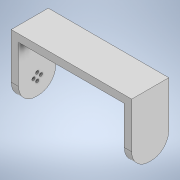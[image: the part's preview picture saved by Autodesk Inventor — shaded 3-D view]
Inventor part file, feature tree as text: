
AUTODESK INVENTOR PART (.ipt)
format: ipt  version: 2022 (Build 260153000, 153)  size: 152,064 bytes
history: native  units: mm
features: extrude x5, sketch x5, fillet x1
ambient origin geometry x8: Origin, YZ Plane, XZ Plane, XY Plane, X Axis, Y Axis, Z Axis, Center Point
bodies: Solid1 (feature_tree)
feature tree (11):
  extrude  "Extrusion1"  Depth=40.0mm
  extrude  "Extrusion3"  Depth=8.0mm
  extrude  "Extrusion4"  TaperAngle=0.0deg  [1 undecoded]
  extrude  "Extrusion6"  Depth=18.0mm
  fillet  "Fillet1"  Radius=3.5mm
  extrude  "Extrusion7"  Depth=8.0mm TaperAngle=0.0deg
  sketch  "Sketch1"  dims[d0=130.0mm d1=40.0mm]
  sketch  "Sketch3"  dims[d2=50.0mm d3=0.0mm d8=8.0mm]
  sketch  "Sketch4"  dims[d9=42.0mm d10=0.0mm d11=0.0mm]
  sketch  "Sketch7"  dims[d12=18.0mm d13=0.0mm d23=18.0mm d25=3.5mm]
  sketch  "Sketch8"  dims[d26=40.0mm d28=360.0deg d30=8.0mm d31=0.0mm d32=18.75mm d33=12.8mm d34=15.0mm d35=0.0mm]
note: 1 required parameter value undecoded (feature->parameter linkage not recoverable at this tier; creation-order binding heuristic only, values carry confidence <= 0.55)
